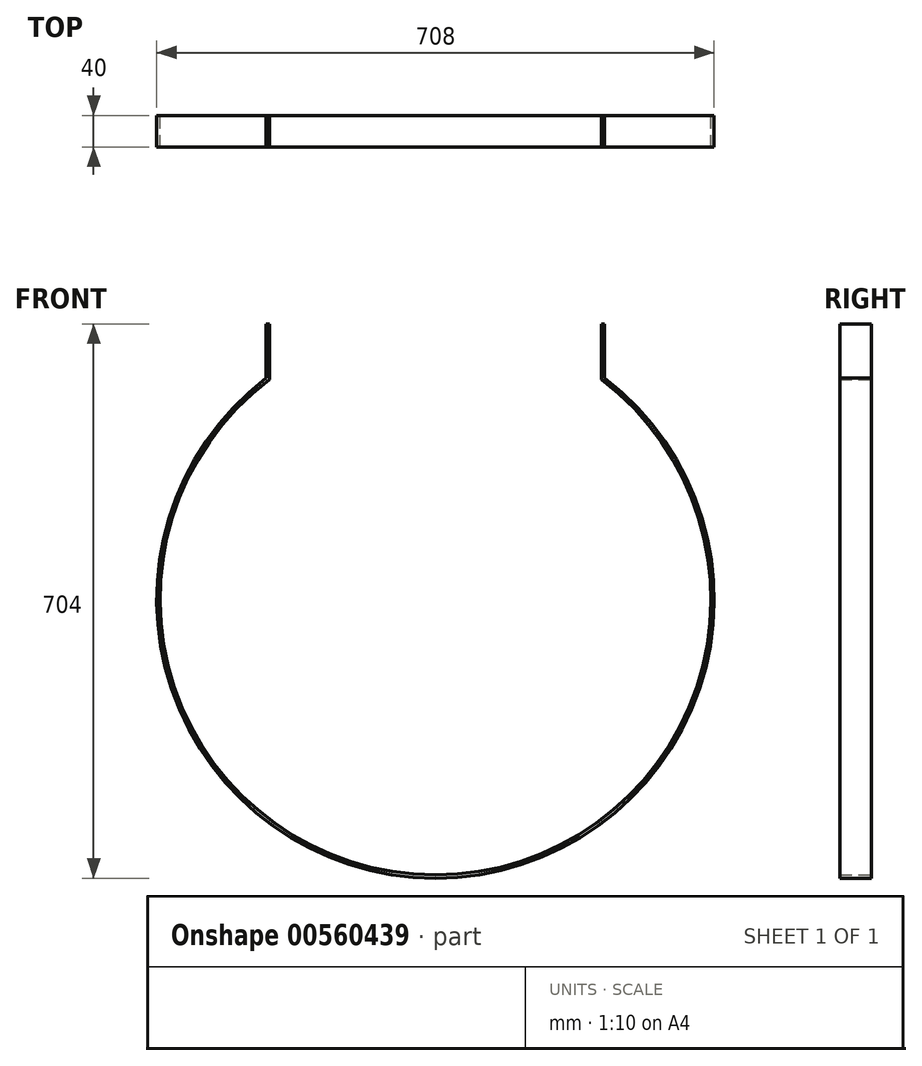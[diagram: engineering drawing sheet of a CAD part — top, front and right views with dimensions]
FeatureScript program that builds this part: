
annotation { "Feature Type Name" : "Feature", "Feature Type Description" : "" }
export const myFeature = defineFeature(function(context is Context, id is Id, definition is map)
    precondition{}
    {
        {
            var Q0;
            Q0=qCreatedBy(makeId("Front.planeOp"),FACE);
            var sketch = newSketch(context, id + "F0", { "sketchPlane" : qUnion([Q0])});
            skLineSegment(sketch, "E0", {"start": v(-422, 0) * mm, "end": v(-422, 350) * mm});
            skLineSegment(sketch, "E1", {"start": v(-211, 350) * mm, "end": v(-211, 279.25) * mm});
            skArc(sketch, "E2", {"start": v(211, 279.25) * mm, "mid": v(0, -350) * mm, "end": v(-211, 279.25) * mm});
            skLineSegment(sketch, "E3", {"start": v(211, 279.25) * mm, "end": v(211, 350) * mm});
            skLineSegment(sketch, "E4.0", {"start": v(-215, 350) * mm, "end": v(-215, 281.23) * mm});
            skArc(sketch, "E4.1", {"start": v(215, 281.24) * mm, "mid": v(0, -354) * mm, "end": v(-215, 281.23) * mm});
            skLineSegment(sketch, "E4.2", {"start": v(215, 281.24) * mm, "end": v(215, 350) * mm});
            skLineSegment(sketch, "E5", {"start": v(-215, 350) * mm, "end": v(-211, 350) * mm});
            skLineSegment(sketch, "E6", {"start": v(211, 350) * mm, "end": v(215, 350) * mm});
            skSolve(sketch);
        }
        {
            var Q0;
            Q0=makeQuery(id+"F0.imprint","IMPRINT",FACE,{"disambiguationData":[TD([[makeQuery(id+"F0.imprint","IMPRINT",EDGE,{"derivedFrom":sQuery(id+"F0.wireOp",EDGE,"E1")}),-1.0]])]});
            extrude(context, id + "F1", {"entities" : qUnion([Q0]), "endBound" : BoundingType.SYMMETRIC, "depth" : 40 * mm, "offsetDistance" : 25 * mm});
        }
    });
